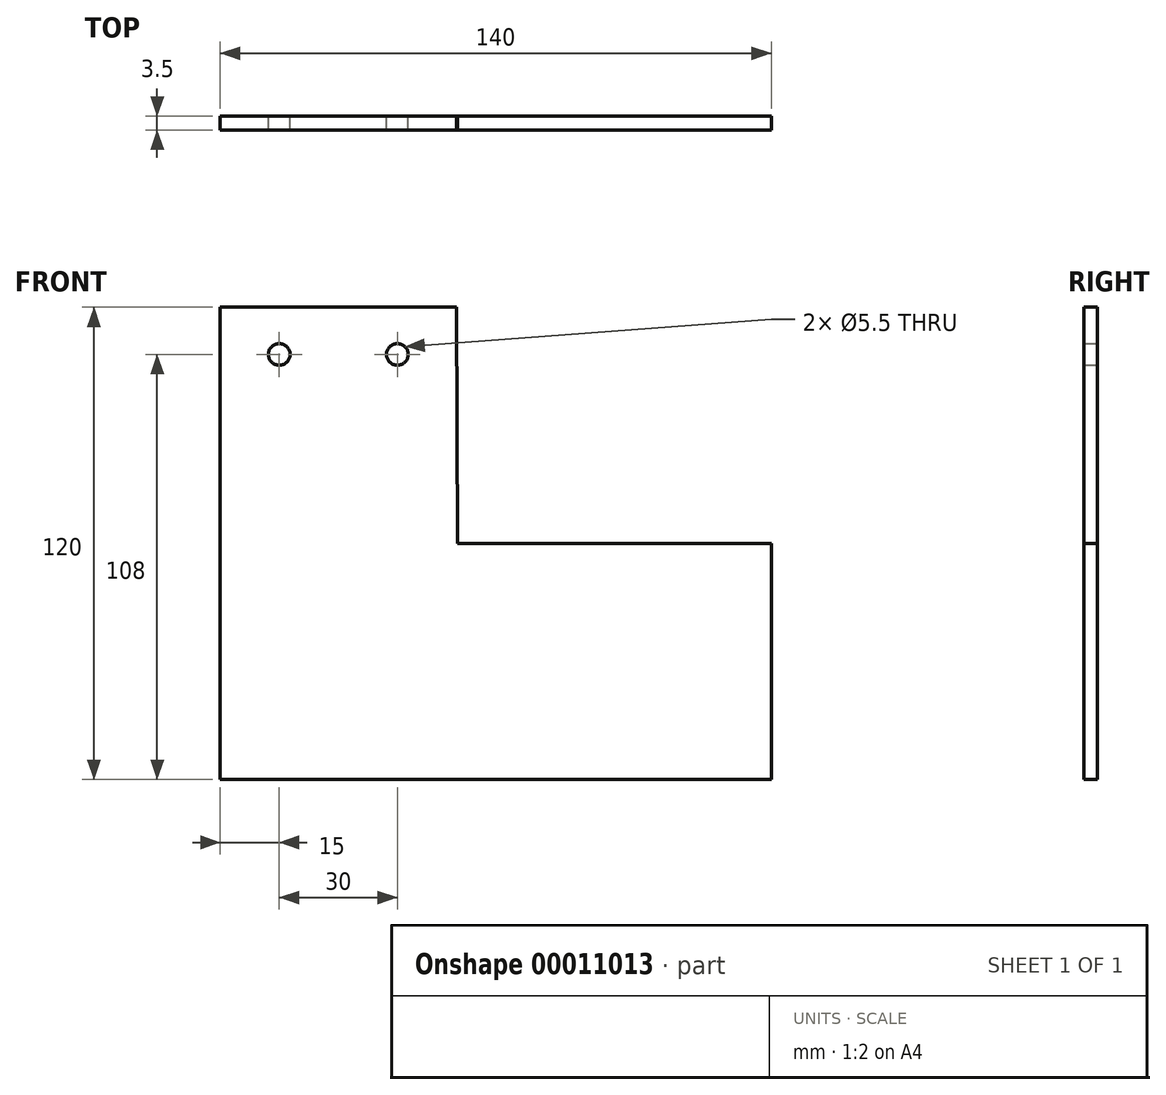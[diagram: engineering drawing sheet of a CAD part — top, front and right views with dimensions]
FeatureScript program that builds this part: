
annotation { "Feature Type Name" : "Feature", "Feature Type Description" : "" }
export const myFeature = defineFeature(function(context is Context, id is Id, definition is map)
    precondition{}
    {
        {
            var Q0;
            Q0=qCreatedBy(makeId("Front.planeOp"),FACE);
            var sketch = newSketch(context, id + "F0", { "sketchPlane" : qUnion([Q0])});
            skLineSegment(sketch, "E0.bottom", {"start": v(70, -60) * mm, "end": v(-70, -60) * mm});
            skLineSegment(sketch, "E0.top", {"start": v(-10, 60) * mm, "end": v(-70, 60) * mm});
            skLineSegment(sketch, "E0.left", {"start": v(70, -60) * mm, "end": v(70, 0) * mm});
            skLineSegment(sketch, "E0.right", {"start": v(-70, -60) * mm, "end": v(-70, 60) * mm});
            skPoint(sketch, "E0.middle", {"position": v(0, 0) * mm});
            skLineSegment(sketch, "E1", {"start": v(-10, 60) * mm, "end": v(-9.77, 0) * mm});
            skLineSegment(sketch, "E2", {"start": v(-9.77, 0) * mm, "end": v(70, 0) * mm});
            skLineSegment(sketch, "E3", {"start": v(-78.28, 48) * mm, "end": v(-2.87, 48) * mm, "construction": true});
            skLineSegment(sketch, "E4", {"start": v(-55, 65.07) * mm, "end": v(-55, 34.64) * mm, "construction": true});
            skLineSegment(sketch, "E5", {"start": v(-25, 65.51) * mm, "end": v(-25, 34.35) * mm, "construction": true});
            skCircle(sketch, "E6", {"center": v(-55, 48) * mm, "radius": 2.75 * mm});
            skCircle(sketch, "E7", {"center": v(-25, 48) * mm, "radius": 2.75 * mm});
            skPoint(sketch, "E8.orphan", {"position": v(70, 60) * mm});
            skSolve(sketch);
        }
        {
            var Q0;
            Q0 = qSketchRegion(id + "F0", true);
            extrude(context, id + "F1", {"entities" : qUnion([Q0]), "depth" : 3.5 * mm, "offsetDistance" : 25 * mm});
        }
    });
